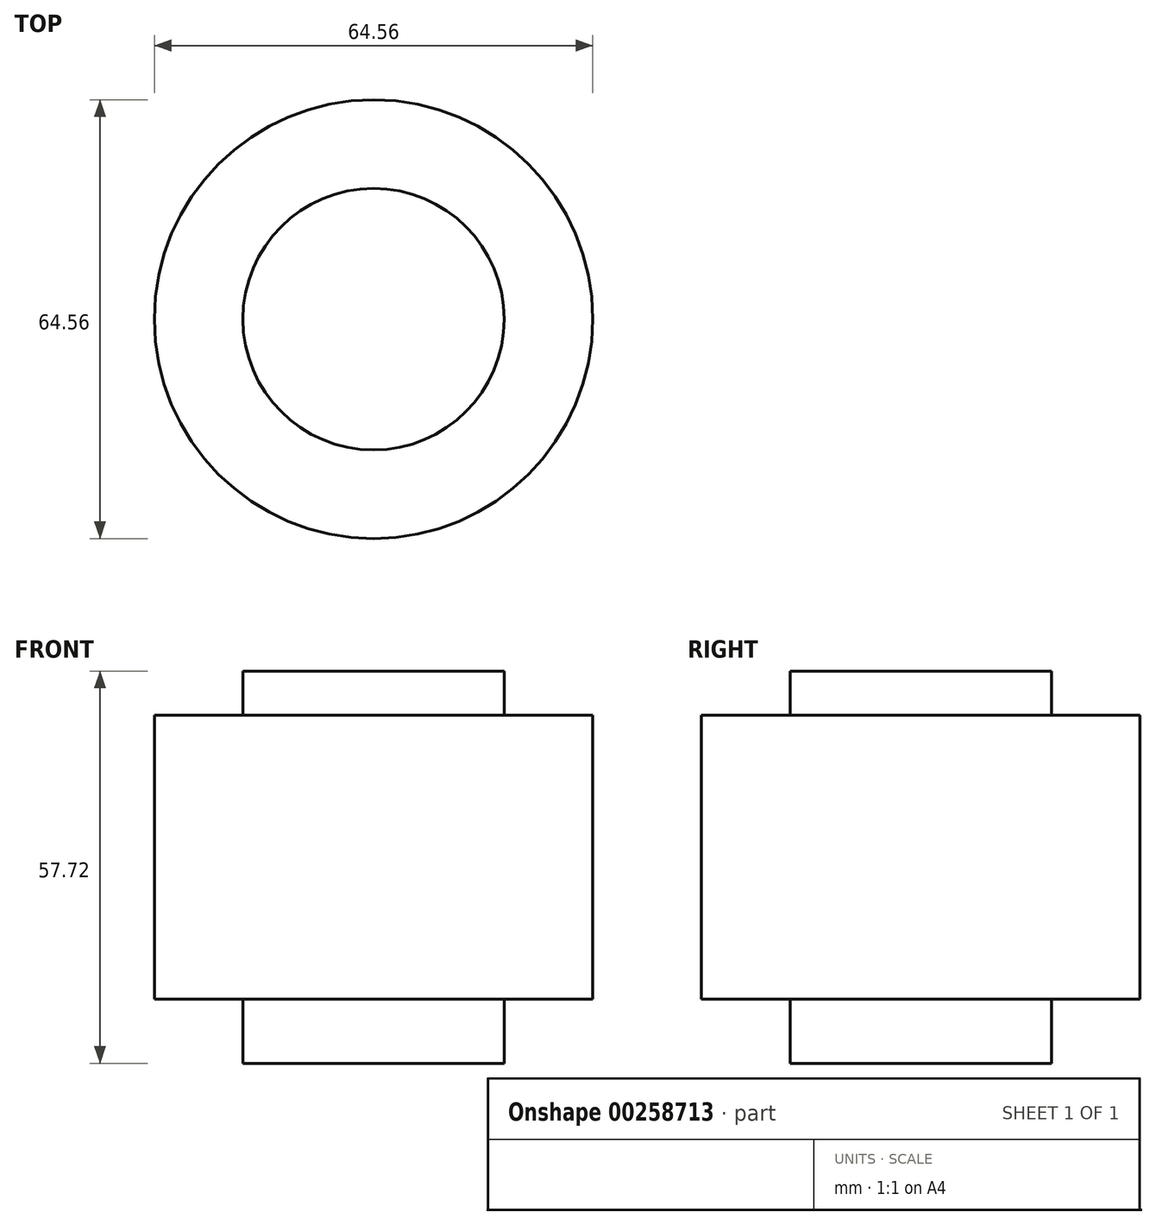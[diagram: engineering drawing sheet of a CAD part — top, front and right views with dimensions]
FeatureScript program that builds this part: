
annotation { "Feature Type Name" : "Feature", "Feature Type Description" : "" }
export const myFeature = defineFeature(function(context is Context, id is Id, definition is map)
    precondition{}
    {
        {
            var Q0;
            Q0=qCreatedBy(makeId("Front.planeOp"),FACE);
            var sketch = newSketch(context, id + "F0", { "sketchPlane" : qUnion([Q0])});
            skLineSegment(sketch, "E0", {"start": v(0, 33.75) * mm, "end": v(-19.24, 33.75) * mm});
            skLineSegment(sketch, "E1", {"start": v(-19.24, 33.75) * mm, "end": v(-19.24, 27.23) * mm});
            skLineSegment(sketch, "E2", {"start": v(-19.24, 27.23) * mm, "end": v(-32.28, 27.23) * mm});
            skLineSegment(sketch, "E3", {"start": v(-32.28, 27.23) * mm, "end": v(-32.28, -14.51) * mm});
            skLineSegment(sketch, "E4", {"start": v(-32.28, -14.51) * mm, "end": v(-19.24, -14.51) * mm});
            skLineSegment(sketch, "E5", {"start": v(-19.24, -14.51) * mm, "end": v(-19.24, -23.97) * mm});
            skLineSegment(sketch, "E6", {"start": v(-19.24, -23.97) * mm, "end": v(0, -23.97) * mm});
            skLineSegment(sketch, "E7", {"start": v(0, -23.97) * mm, "end": v(0, 33.75) * mm});
            skSolve(sketch);
        }
        {
            var Q0;
            Q0 = qSketchRegion(id + "F0", true);
            var Q1;
            Q1=sQuery(id+"F0.wireOp",EDGE,"E7");
            revolve(context, id + "F1", {"entities" : qUnion([Q0]), "axis" : qUnion([Q1]), "revolveType" : RevolveType.FULL});
        }
    });
